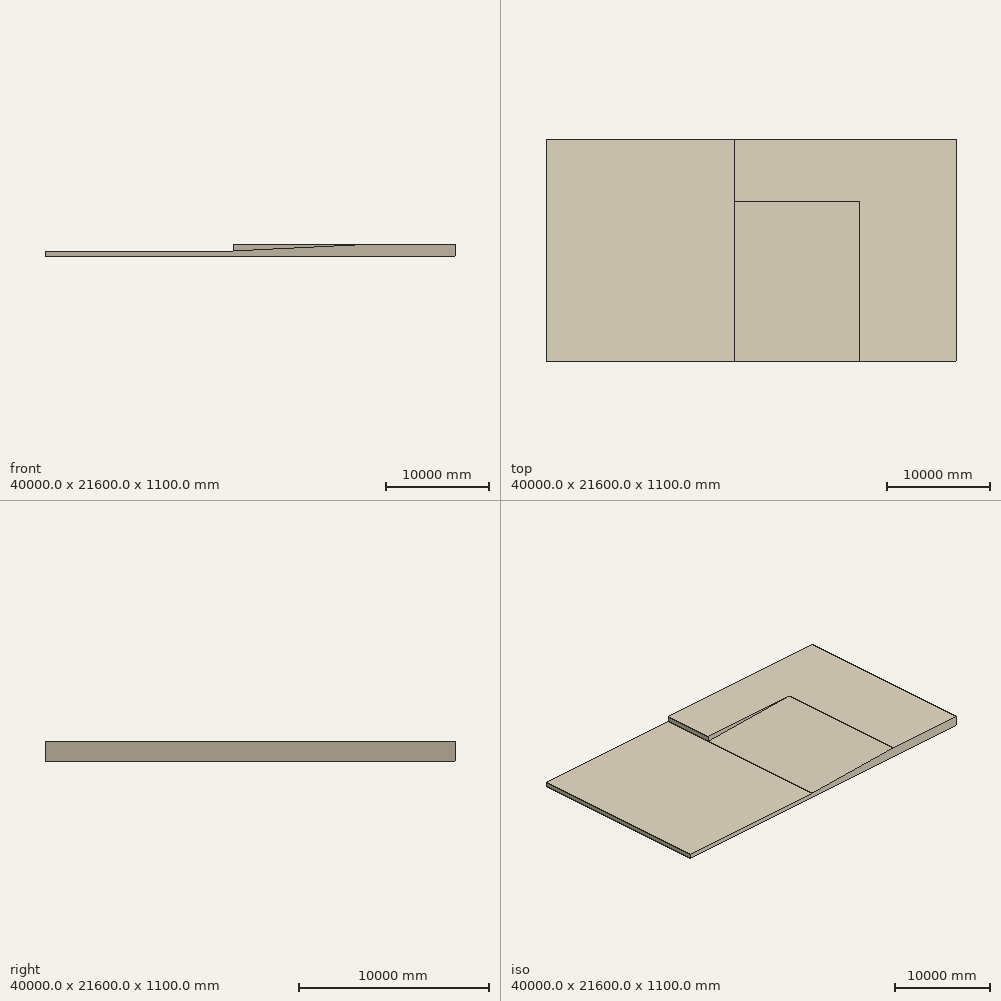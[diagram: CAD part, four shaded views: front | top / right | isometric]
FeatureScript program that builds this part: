
annotation { "Feature Type Name" : "Feature", "Feature Type Description" : "" }
export const myFeature = defineFeature(function(context is Context, id is Id, definition is map)
    precondition{}
    {
        {
            var Q0;
            Q0=qCreatedBy(makeId("Top.planeOp"),FACE);
            var sketch = newSketch(context, id + "F0", { "sketchPlane" : qUnion([Q0])});
            skLineSegment(sketch, "E0.bottom", {"start": v(0, 0) * mm, "end": v(40000, 0) * mm});
            skLineSegment(sketch, "E0.top", {"start": v(0, -21600) * mm, "end": v(40000, -21600) * mm});
            skLineSegment(sketch, "E0.left", {"start": v(0, 0) * mm, "end": v(0, -21600) * mm});
            skLineSegment(sketch, "E0.right", {"start": v(40000, 0) * mm, "end": v(40000, -21600) * mm});
            skSolve(sketch);
        }
        {
            var Q0;
            Q0 = qSketchRegion(id + "F0", true);
            extrude(context, id + "F1", {"entities" : qUnion([Q0]), "depth" : 500 * mm, "offsetDistance" : 25 * mm});
        }
        {
            var Q0;
            Q0=makeQuery(id+"F1.opExtrude","CAP_FACE",FACE,{"disambiguationData":[OSD([sQuery(id+"F0.wireOp",EDGE,"E0.bottom"),sQuery(id+"F0.wireOp",EDGE,"E0.top"),sQuery(id+"F0.wireOp",EDGE,"E0.left"),sQuery(id+"F0.wireOp",EDGE,"E0.right")])],"isStart":false});
            var sketch = newSketch(context, id + "F2", { "sketchPlane" : qUnion([Q0])});
            skLineSegment(sketch, "E1.bottom", {"start": v(18300, 0) * mm, "end": v(40000, 0) * mm});
            skLineSegment(sketch, "E1.top", {"start": v(18300, -21600) * mm, "end": v(40000, -21600) * mm});
            skLineSegment(sketch, "E1.left", {"start": v(18300, 0) * mm, "end": v(18300, -21600) * mm});
            skLineSegment(sketch, "E1.right", {"start": v(40000, 0) * mm, "end": v(40000, -21600) * mm});
            skSolve(sketch);
        }
        {
            var Q0;
            Q0 = qSketchRegion(id + "F2", true);
            extrude(context, id + "F3", {"entities" : qUnion([Q0]), "operationType" : NewBodyOperationType.ADD, "depth" : 600 * mm, "offsetDistance" : 25 * mm});
        }
        {
            var Q0;
            Q0=makeQuery(id+"F3.boolean.opBoolean","MERGE",FACE,{"derivedFrom":[makeQuery(id+"F1.opExtrude","SWEPT_FACE",FACE,{"disambiguationData":[OSD([sQuery(id+"F0.wireOp",EDGE,"E0.top")])]}),makeQuery(id+"F3.opExtrude","SWEPT_FACE",FACE,{"disambiguationData":[OSD([sQuery(id+"F2.wireOp",EDGE,"E1.top")])]})]});
            var sketch = newSketch(context, id + "F4", { "sketchPlane" : qUnion([Q0])});
            skLineSegment(sketch, "E2", {"start": v(18300, 1100) * mm, "end": v(30500, 1100) * mm});
            skLineSegment(sketch, "E3", {"start": v(30500, 1100) * mm, "end": v(18300, 500) * mm});
            skLineSegment(sketch, "E4", {"start": v(18300, 500) * mm, "end": v(18300, 1100) * mm});
            skSolve(sketch);
        }
        {
            var Q0;
            Q0 = qSketchRegion(id + "F4", true);
            extrude(context, id + "F5", {"entities" : qUnion([Q0]), "operationType" : NewBodyOperationType.REMOVE, "oppositeDirection" : true, "depth" : 15600 * mm, "offsetDistance" : 25 * mm});
        }
    });
